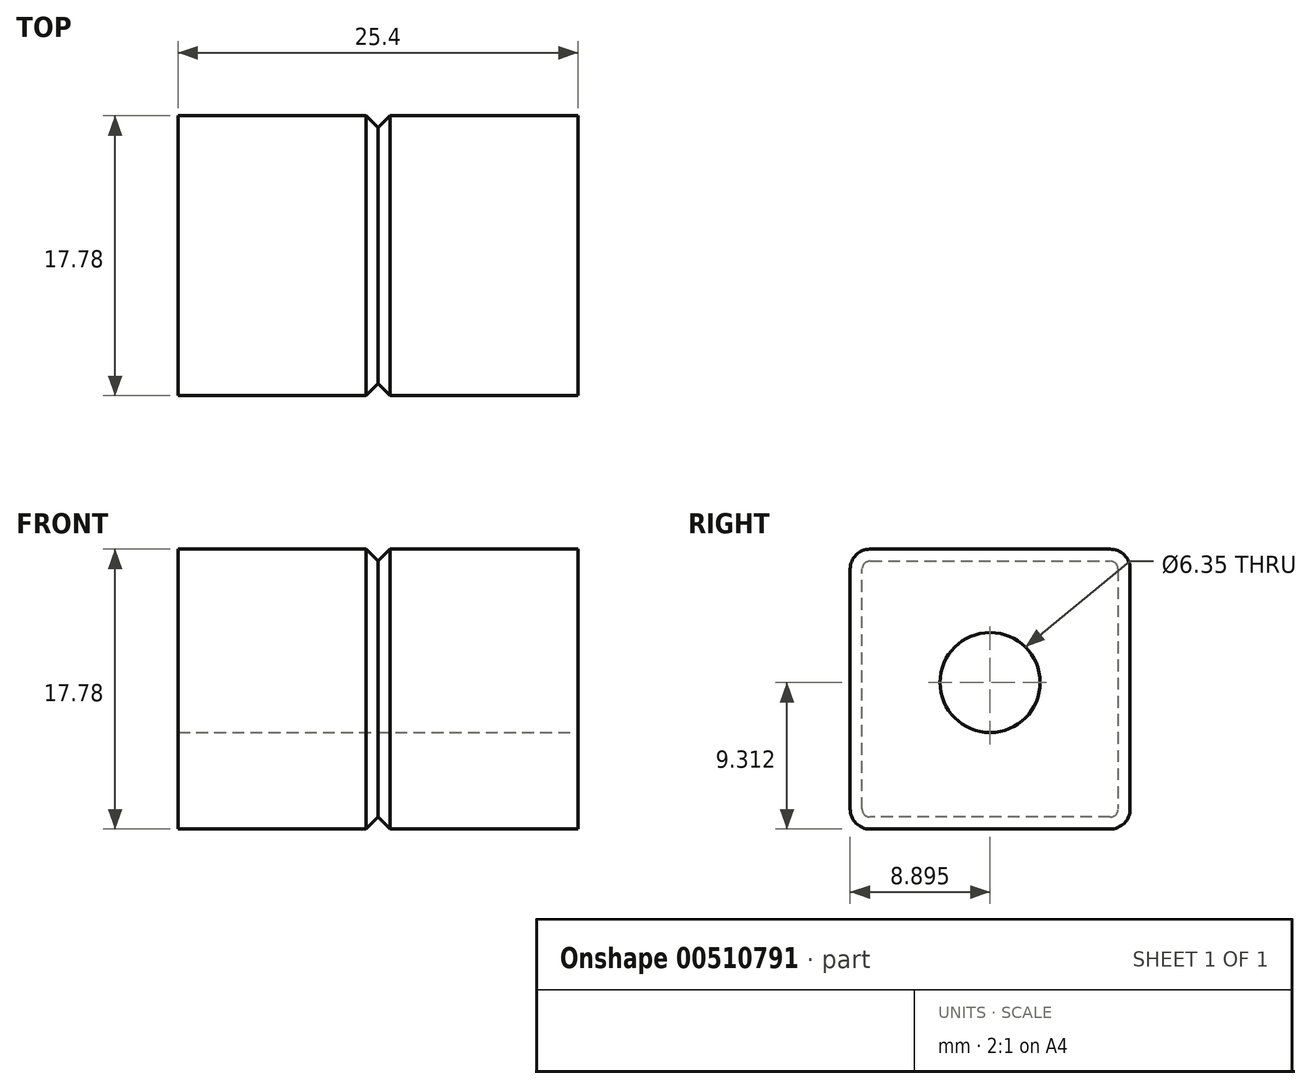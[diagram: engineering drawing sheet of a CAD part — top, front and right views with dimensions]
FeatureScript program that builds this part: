
annotation { "Feature Type Name" : "Feature", "Feature Type Description" : "" }
export const myFeature = defineFeature(function(context is Context, id is Id, definition is map)
    precondition{}
    {
        {
            var Q0;
            Q0=qCreatedBy(makeId("Right.planeOp"),FACE);
            var sketch = newSketch(context, id + "F0", { "sketchPlane" : qUnion([Q0])});
            skLineSegment(sketch, "E0", {"start": v(-46.4, 45.36) * mm, "end": v(-46.4, 30.12) * mm});
            skLineSegment(sketch, "E1", {"start": v(-45.13, 28.85) * mm, "end": v(-29.89, 28.85) * mm});
            skLineSegment(sketch, "E2", {"start": v(-28.62, 30.12) * mm, "end": v(-28.62, 45.36) * mm});
            skLineSegment(sketch, "E3", {"start": v(-29.89, 46.63) * mm, "end": v(-45.13, 46.63) * mm});
            skPoint(sketch, "E4.visualSharp", {"position": v(-46.4, 46.63) * mm});
            skArc(sketch, "E4.filletArc", {"start": v(-45.13, 46.63) * mm, "mid": v(-46.02, 46.26) * mm, "end": v(-46.4, 45.36) * mm});
            skPoint(sketch, "E5.visualSharp", {"position": v(-28.62, 46.63) * mm});
            skArc(sketch, "E5.filletArc", {"start": v(-28.62, 45.36) * mm, "mid": v(-28.99, 46.26) * mm, "end": v(-29.89, 46.63) * mm});
            skPoint(sketch, "E6.visualSharp", {"position": v(-46.4, 28.85) * mm});
            skArc(sketch, "E6.filletArc", {"start": v(-46.4, 30.12) * mm, "mid": v(-46.02, 29.23) * mm, "end": v(-45.13, 28.85) * mm});
            skPoint(sketch, "E7.visualSharp", {"position": v(-28.62, 28.85) * mm});
            skArc(sketch, "E7.filletArc", {"start": v(-29.89, 28.85) * mm, "mid": v(-28.99, 29.23) * mm, "end": v(-28.62, 30.12) * mm});
            skSolve(sketch);
        }
        {
            var Q0;
            Q0 = qSketchRegion(id + "F0", true);
            extrude(context, id + "F1", {"entities" : qUnion([Q0]), "depth" : 12.7 * mm, "offsetDistance" : 25.4 * mm});
        }
        {
            var Q0;
            Q0=makeQuery(id+"F1.opExtrude","CAP_EDGE",EDGE,{"disambiguationData":[OSD([sQuery(id+"F0.wireOp",EDGE,"E3")])],"isStart":true});
            var Q1;
            Q1=makeQuery(id+"F1.opExtrude","CAP_EDGE",EDGE,{"disambiguationData":[OSD([sQuery(id+"F0.wireOp",EDGE,"E0")])],"isStart":true});
            chamfer(context, id + "F2", {"entities" : qUnion([Q0, Q1]), "width" : 0.76 * mm, "tangentPropagation" : true});
        }
        {
            var Q0;
            Q0=makeQuery(id+"F1.opExtrude","SWEPT_BODY",BODY,{"disambiguationData":[OSD([sQuery(id+"F0.wireOp",EDGE,"E0"),sQuery(id+"F0.wireOp",EDGE,"E1"),sQuery(id+"F0.wireOp",EDGE,"E2"),sQuery(id+"F0.wireOp",EDGE,"E3"),sQuery(id+"F0.wireOp",EDGE,"E4.filletArc"),sQuery(id+"F0.wireOp",EDGE,"E5.filletArc"),sQuery(id+"F0.wireOp",EDGE,"E6.filletArc"),sQuery(id+"F0.wireOp",EDGE,"E7.filletArc")])]});
            var Q1;
            Q1=qCreatedBy(makeId("Right.planeOp"),FACE);
            mirror(context, id + "F3", {"operationType" : NewBodyOperationType.ADD, "entities" : qUnion([Q0]), "mirrorPlane" : qUnion([Q1])});
        }
        {
            var Q0;
            Q0=makeQuery(id+"F1.opExtrude","CAP_FACE",FACE,{"disambiguationData":[OSD([sQuery(id+"F0.wireOp",EDGE,"E0"),sQuery(id+"F0.wireOp",EDGE,"E1"),sQuery(id+"F0.wireOp",EDGE,"E2"),sQuery(id+"F0.wireOp",EDGE,"E3"),sQuery(id+"F0.wireOp",EDGE,"E4.filletArc"),sQuery(id+"F0.wireOp",EDGE,"E5.filletArc"),sQuery(id+"F0.wireOp",EDGE,"E6.filletArc"),sQuery(id+"F0.wireOp",EDGE,"E7.filletArc")])],"isStart":false});
            var sketch = newSketch(context, id + "F4", { "sketchPlane" : qUnion([Q0])});
            skCircle(sketch, "E8", {"center": v(-37.5, 38.16) * mm, "radius": 3.18 * mm});
            skPoint(sketch, "E8.centerSnap0", {"position": v(-37.5, 46.63) * mm});
            skSolve(sketch);
        }
        {
            var Q0;
            Q0=makeQuery(id+"F4.imprint","IMPRINT",FACE,{"disambiguationData":[TD([[makeQuery(id+"F4.imprint","IMPRINT",EDGE,{"derivedFrom":sQuery(id+"F4.wireOp",EDGE,"E8")}),1.0]])]});
            extrude(context, id + "F5", {"entities" : qUnion([Q0]), "operationType" : NewBodyOperationType.REMOVE, "endBound" : BoundingType.THROUGH_ALL, "oppositeDirection" : true, "depth" : 25.4 * mm, "offsetDistance" : 25.4 * mm});
        }
    });
